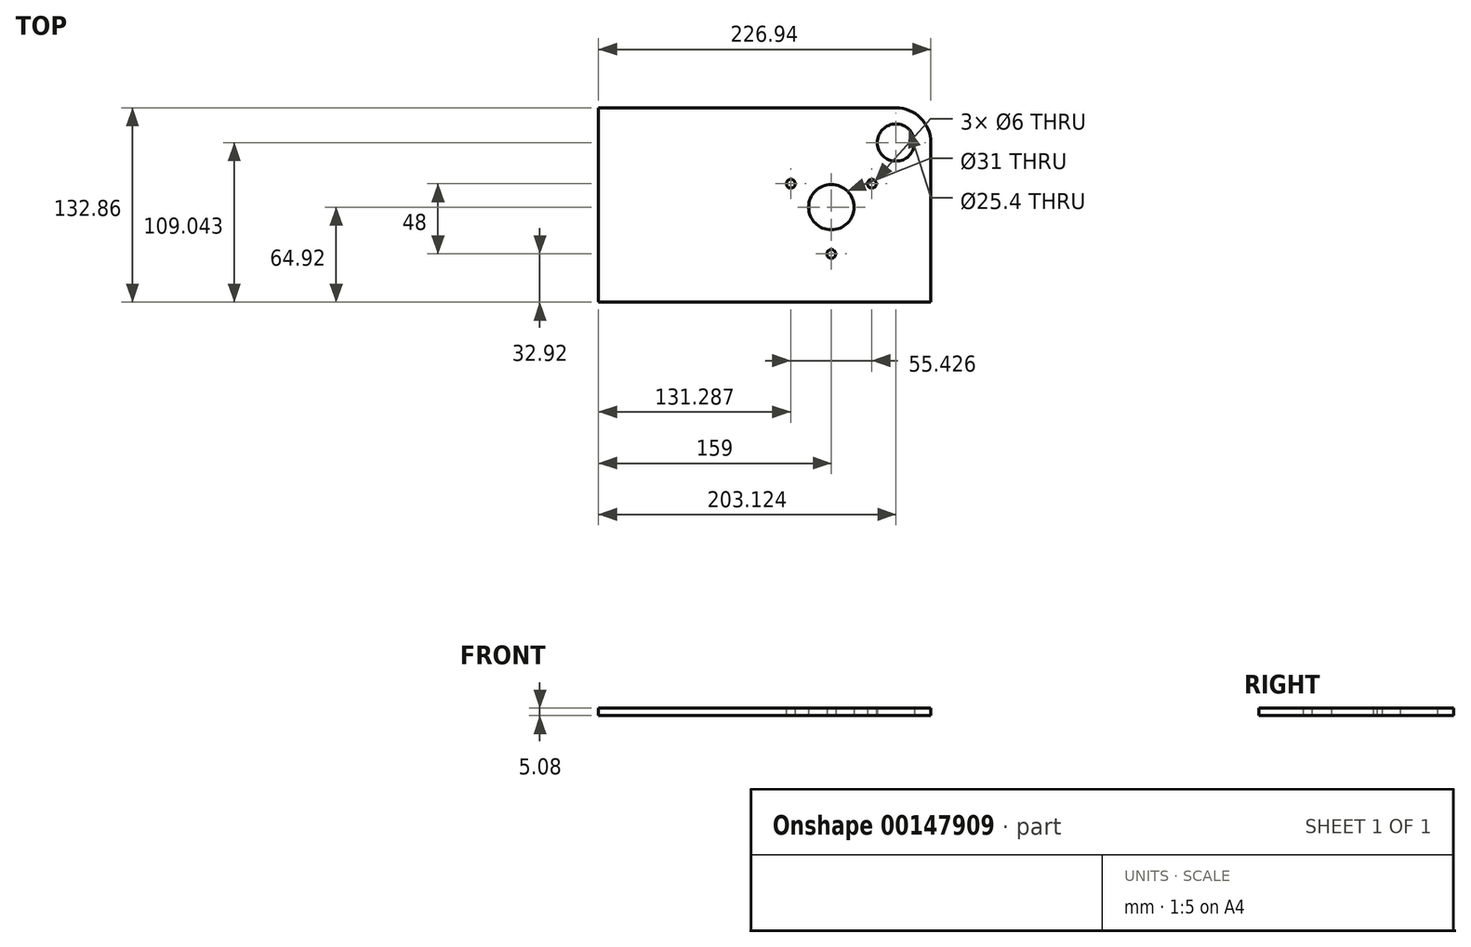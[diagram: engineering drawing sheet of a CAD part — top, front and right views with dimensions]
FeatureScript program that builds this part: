
annotation { "Feature Type Name" : "Feature", "Feature Type Description" : "" }
export const myFeature = defineFeature(function(context is Context, id is Id, definition is map)
    precondition{}
    {
        {
            var Q0;
            Q0=qCreatedBy(makeId("Top.planeOp"),FACE);
            var sketch = newSketch(context, id + "F0", { "sketchPlane" : qUnion([Q0])});
            skLineSegment(sketch, "E0", {"start": v(0, 0) * mm, "end": v(0, -32) * mm, "construction": true});
            skLineSegment(sketch, "E1", {"start": v(0, 0) * mm, "end": v(-27.71, 16) * mm, "construction": true});
            skLineSegment(sketch, "E2", {"start": v(0, 0) * mm, "end": v(27.71, 16) * mm, "construction": true});
            skLineSegment(sketch, "E3", {"start": v(0, -32) * mm, "end": v(-27.71, 16) * mm, "construction": true});
            skLineSegment(sketch, "E4", {"start": v(-27.71, 16) * mm, "end": v(27.71, 16) * mm, "construction": true});
            skLineSegment(sketch, "E5", {"start": v(27.71, 16) * mm, "end": v(0, -32) * mm, "construction": true});
            skCircle(sketch, "E6", {"center": v(0, 0) * mm, "radius": 15.5 * mm});
            skCircle(sketch, "E7", {"center": v(0, -32) * mm, "radius": 3 * mm});
            skCircle(sketch, "E8", {"center": v(27.71, 16) * mm, "radius": 3 * mm});
            skCircle(sketch, "E9", {"center": v(-27.71, 16) * mm, "radius": 3 * mm});
            skLineSegment(sketch, "E10", {"start": v(0, 0) * mm, "end": v(44.12, 0) * mm, "construction": true});
            skLineSegment(sketch, "E11", {"start": v(44.12, 0) * mm, "end": v(44.12, 44.12) * mm, "construction": true});
            skLineSegment(sketch, "E12", {"start": v(44.12, 44.12) * mm, "end": v(0, 0) * mm, "construction": true});
            skCircle(sketch, "E13", {"center": v(44.12, 44.12) * mm, "radius": 12.7 * mm});
            skLineSegment(sketch, "E14.bottom", {"start": v(-159, 67.94) * mm, "end": v(67.94, 67.94) * mm});
            skLineSegment(sketch, "E14.top", {"start": v(-159, -64.92) * mm, "end": v(67.94, -64.92) * mm});
            skLineSegment(sketch, "E14.left", {"start": v(-159, 67.94) * mm, "end": v(-159, -64.92) * mm});
            skLineSegment(sketch, "E14.right", {"start": v(67.94, 67.94) * mm, "end": v(67.94, -64.92) * mm});
            skLineSegment(sketch, "E15", {"start": v(44.12, 0) * mm, "end": v(44.12, -64.92) * mm, "construction": true});
            skLineSegment(sketch, "E16", {"start": v(0, 0) * mm, "end": v(-159, 0) * mm, "construction": true});
            skLineSegment(sketch, "E17", {"start": v(44.12, 44.12) * mm, "end": v(44.12, 67.94) * mm, "construction": true});
            skLineSegment(sketch, "E18", {"start": v(44.12, 44.12) * mm, "end": v(67.94, 44.12) * mm, "construction": true});
            skSolve(sketch);
        }
        {
            var Q0;
            Q0=qSketchRegion(id+"F0",true);
            extrude(context, id + "F1", {"entities" : qUnion([Q0]), "depth" : 5.08 * mm});
        }
        {
            var Q0;
            Q0=makeQuery(id+"F1.opExtrude","SWEPT_EDGE",EDGE,{"disambiguationData":[OSD([sQuery(id+"F0.wireOp",EDGE,"E14.bottom"),sQuery(id+"F0.wireOp",EDGE,"E14.right")])]});
            fillet(context, id + "F2", {"entities" : qUnion([Q0]), "radius" : 23.8 * mm, "tangentPropagation" : true, "allowEdgeOverflow" : false});
        }
    });
